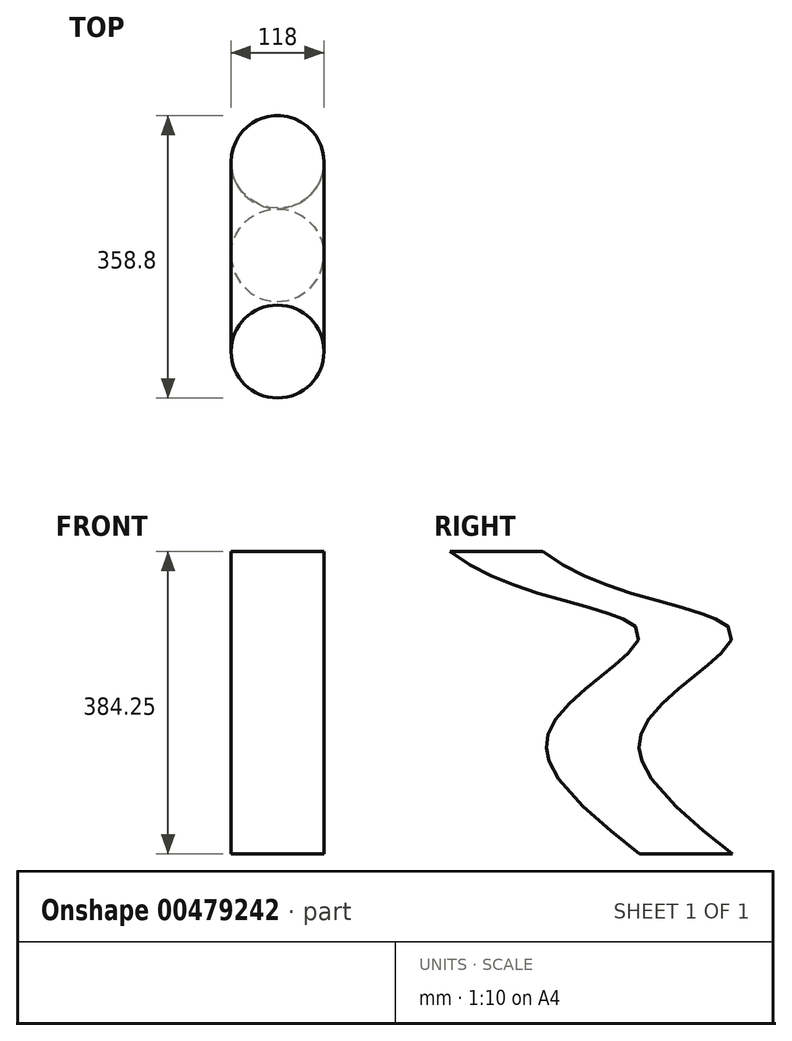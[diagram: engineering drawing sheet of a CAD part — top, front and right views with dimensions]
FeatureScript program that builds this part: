
annotation { "Feature Type Name" : "Feature", "Feature Type Description" : "" }
export const myFeature = defineFeature(function(context is Context, id is Id, definition is map)
    precondition{}
    {
        {
            var Q0;
            Q0=qCreatedBy(makeId("Top.planeOp"),FACE);
            var sketch = newSketch(context, id + "F0", { "sketchPlane" : qUnion([Q0])});
            skCircle(sketch, "E0", {"center": v(0, 0) * mm, "radius": 59 * mm});
            skSolve(sketch);
        }
        {
            var Q0;
            Q0=qCreatedBy(makeId("Right.planeOp"),FACE);
            var sketch = newSketch(context, id + "F1", { "sketchPlane" : qUnion([Q0])});
            skFitSpline(sketch, "E1", {"points": [v(0, 0) * mm, v(-114.08, 158.13) * mm, v(0, 279.14) * mm, v(-240.76, 384.25) * mm], "startDerivative": vector(-653.96, 526) * mm, "endDerivative": vector(-660.16, 522.52) * mm});
            skSolve(sketch);
        }
        {
            var Q0;
            Q0=makeQuery(id+"F0.imprint","IMPRINT",FACE,{"disambiguationData":[TD([[makeQuery(id+"F0.imprint","IMPRINT",EDGE,{"derivedFrom":sQuery(id+"F0.wireOp",EDGE,"E0")}),1.0]])]});
            var Q1;
            Q1=sQuery(id+"F1.wireOp",EDGE,"E1");
            sweep(context, id + "F2", {"profiles" : qUnion([Q0]), "path" : qUnion([Q1]), "keepProfileOrientation" : true});
        }
    });
